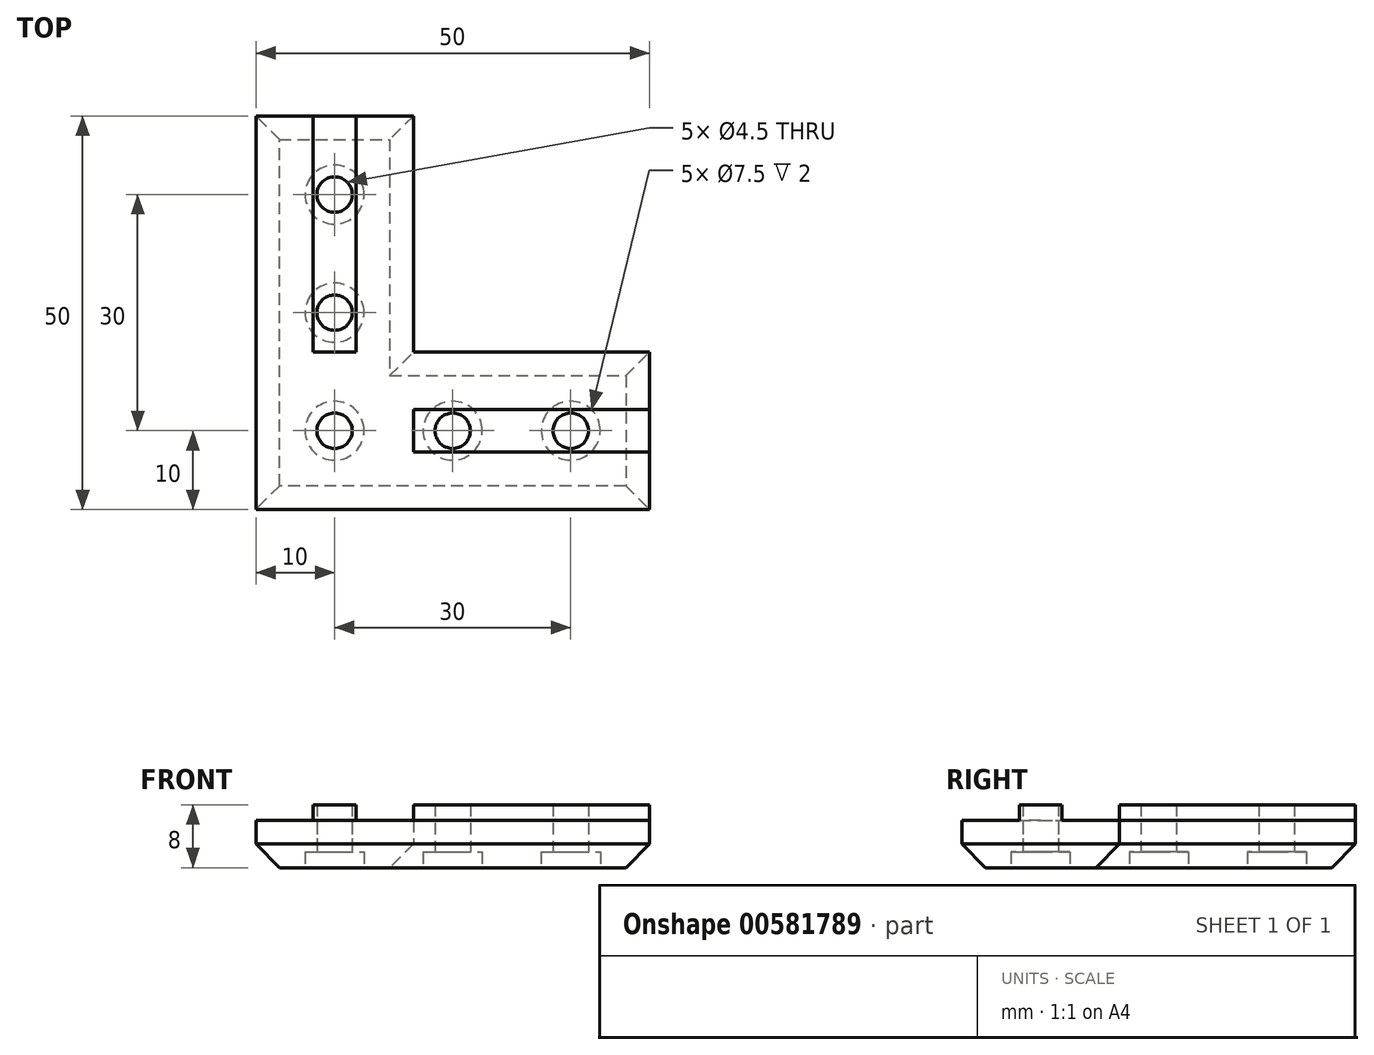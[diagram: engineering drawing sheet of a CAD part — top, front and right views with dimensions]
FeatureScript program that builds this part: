
annotation { "Feature Type Name" : "Feature", "Feature Type Description" : "" }
export const myFeature = defineFeature(function(context is Context, id is Id, definition is map)
    precondition{}
    {
        {
            var Q0;
            Q0=qCreatedBy(makeId("Top.planeOp"),FACE);
            var sketch = newSketch(context, id + "F0", { "sketchPlane" : qUnion([Q0])});
            skLineSegment(sketch, "E0", {"start": v(0, 0) * mm, "end": v(0, 50) * mm});
            skLineSegment(sketch, "E1", {"start": v(0, 50) * mm, "end": v(20, 50) * mm});
            skLineSegment(sketch, "E2", {"start": v(20, 50) * mm, "end": v(20, 20) * mm});
            skLineSegment(sketch, "E3", {"start": v(20, 20) * mm, "end": v(50, 20) * mm});
            skLineSegment(sketch, "E4", {"start": v(50, 20) * mm, "end": v(50, 0) * mm});
            skLineSegment(sketch, "E5", {"start": v(50, 0) * mm, "end": v(0, 0) * mm});
            skSolve(sketch);
        }
        {
            var Q0;
            Q0=qSketchRegion(id+"F0",true);
            extrude(context, id + "F1", {"entities" : qUnion([Q0]), "depth" : 6 * mm});
        }
        {
            var Q0;
            Q0=makeQuery(id+"F1.opExtrude","CAP_FACE",FACE,{"disambiguationData":[OSD([sQuery(id+"F0.wireOp",EDGE,"E0"),sQuery(id+"F0.wireOp",EDGE,"E1"),sQuery(id+"F0.wireOp",EDGE,"E2"),sQuery(id+"F0.wireOp",EDGE,"E3"),sQuery(id+"F0.wireOp",EDGE,"E4"),sQuery(id+"F0.wireOp",EDGE,"E5")])],"isStart":false});
            var sketch = newSketch(context, id + "F2", { "sketchPlane" : qUnion([Q0])});
            skLineSegment(sketch, "E6", {"start": v(7.3, 50) * mm, "end": v(12.71, 50) * mm});
            skLineSegment(sketch, "E7", {"start": v(12.71, 50) * mm, "end": v(12.71, 20) * mm});
            skLineSegment(sketch, "E8", {"start": v(12.71, 20) * mm, "end": v(10, 20) * mm});
            skPoint(sketch, "E8.endSnap0", {"position": v(10, 50) * mm});
            skLineSegment(sketch, "E9", {"start": v(10, 20) * mm, "end": v(7.3, 20) * mm});
            skLineSegment(sketch, "E10", {"start": v(7.3, 20) * mm, "end": v(7.3, 50) * mm});
            skLineSegment(sketch, "E11", {"start": v(50, 12.7) * mm, "end": v(50, 7.3) * mm});
            skLineSegment(sketch, "E12", {"start": v(50, 7.3) * mm, "end": v(20, 7.3) * mm});
            skLineSegment(sketch, "E13", {"start": v(20, 7.3) * mm, "end": v(20, 10) * mm});
            skPoint(sketch, "E13.endSnap0", {"position": v(50, 10) * mm});
            skLineSegment(sketch, "E14", {"start": v(20, 10) * mm, "end": v(20, 12.71) * mm});
            skLineSegment(sketch, "E15", {"start": v(20, 12.71) * mm, "end": v(50, 12.71) * mm});
            skSolve(sketch);
        }
        {
            var Q0;
            Q0=qSketchRegion(id+"F2",true);
            extrude(context, id + "F3", {"entities" : qUnion([Q0]), "operationType" : NewBodyOperationType.ADD, "depth" : 2 * mm});
        }
        {
            var Q0;
            Q0=makeQuery(id+"F1.opExtrude","CAP_FACE",FACE,{"disambiguationData":[OSD([sQuery(id+"F0.wireOp",EDGE,"E0"),sQuery(id+"F0.wireOp",EDGE,"E1"),sQuery(id+"F0.wireOp",EDGE,"E2"),sQuery(id+"F0.wireOp",EDGE,"E3"),sQuery(id+"F0.wireOp",EDGE,"E4"),sQuery(id+"F0.wireOp",EDGE,"E5")])],"isStart":true});
            var sketch = newSketch(context, id + "F4", { "sketchPlane" : qUnion([Q0])});
            skCircle(sketch, "E16", {"center": v(10, -10) * mm, "radius": 2.25 * mm});
            skCircle(sketch, "E17", {"center": v(40, -10) * mm, "radius": 2.25 * mm});
            skCircle(sketch, "E18", {"center": v(10, -40) * mm, "radius": 2.25 * mm});
            skCircle(sketch, "E19", {"center": v(25, -10) * mm, "radius": 2.25 * mm});
            skCircle(sketch, "E20", {"center": v(10, -25) * mm, "radius": 2.25 * mm});
            skSolve(sketch);
        }
        {
            var Q0;
            Q0=qSketchRegion(id+"F4",true);
            extrude(context, id + "F5", {"entities" : qUnion([Q0]), "operationType" : NewBodyOperationType.REMOVE, "endBound" : BoundingType.THROUGH_ALL, "oppositeDirection" : true, "depth" : 25 * mm});
        }
        {
            var Q0;
            Q0=makeQuery(id+"F1.opExtrude","CAP_FACE",FACE,{"disambiguationData":[OSD([sQuery(id+"F0.wireOp",EDGE,"E0"),sQuery(id+"F0.wireOp",EDGE,"E1"),sQuery(id+"F0.wireOp",EDGE,"E2"),sQuery(id+"F0.wireOp",EDGE,"E3"),sQuery(id+"F0.wireOp",EDGE,"E4"),sQuery(id+"F0.wireOp",EDGE,"E5")])],"isStart":true});
            var sketch = newSketch(context, id + "F6", { "sketchPlane" : qUnion([Q0])});
            skCircle(sketch, "E21", {"center": v(10, -10) * mm, "radius": 3.75 * mm});
            skCircle(sketch, "E22", {"center": v(25, -10) * mm, "radius": 3.75 * mm});
            skCircle(sketch, "E23", {"center": v(40, -10) * mm, "radius": 3.75 * mm});
            skCircle(sketch, "E24", {"center": v(10, -25) * mm, "radius": 3.75 * mm});
            skCircle(sketch, "E25", {"center": v(10, -40) * mm, "radius": 3.75 * mm});
            skSolve(sketch);
        }
        {
            var Q0;
            Q0=qSketchRegion(id+"F6",true);
            extrude(context, id + "F7", {"entities" : qUnion([Q0]), "operationType" : NewBodyOperationType.REMOVE, "oppositeDirection" : true, "depth" : 2 * mm});
        }
        {
            var Q0;
            Q0=makeQuery(id+"F1.opExtrude","CAP_EDGE",EDGE,{"disambiguationData":[OSD([sQuery(id+"F0.wireOp",EDGE,"E5")])],"isStart":true});
            var Q1;
            Q1=makeQuery(id+"F1.opExtrude","CAP_EDGE",EDGE,{"disambiguationData":[OSD([sQuery(id+"F0.wireOp",EDGE,"E0")])],"isStart":true});
            var Q2;
            Q2=makeQuery(id+"F1.opExtrude","CAP_EDGE",EDGE,{"disambiguationData":[OSD([sQuery(id+"F0.wireOp",EDGE,"E2")])],"isStart":true});
            var Q3;
            Q3=makeQuery(id+"F1.opExtrude","CAP_EDGE",EDGE,{"disambiguationData":[OSD([sQuery(id+"F0.wireOp",EDGE,"E3")])],"isStart":true});
            var Q4;
            Q4=makeQuery(id+"F1.opExtrude","CAP_EDGE",EDGE,{"disambiguationData":[OSD([sQuery(id+"F0.wireOp",EDGE,"E4")])],"isStart":true});
            var Q5;
            Q5=makeQuery(id+"F1.opExtrude","CAP_EDGE",EDGE,{"disambiguationData":[OSD([sQuery(id+"F0.wireOp",EDGE,"E1")])],"isStart":true});
            chamfer(context, id + "F8", {"entities" : qUnion([Q0, Q1, Q2, Q3, Q4, Q5]), "width" : 3 * mm, "tangentPropagation" : true});
        }
    });
